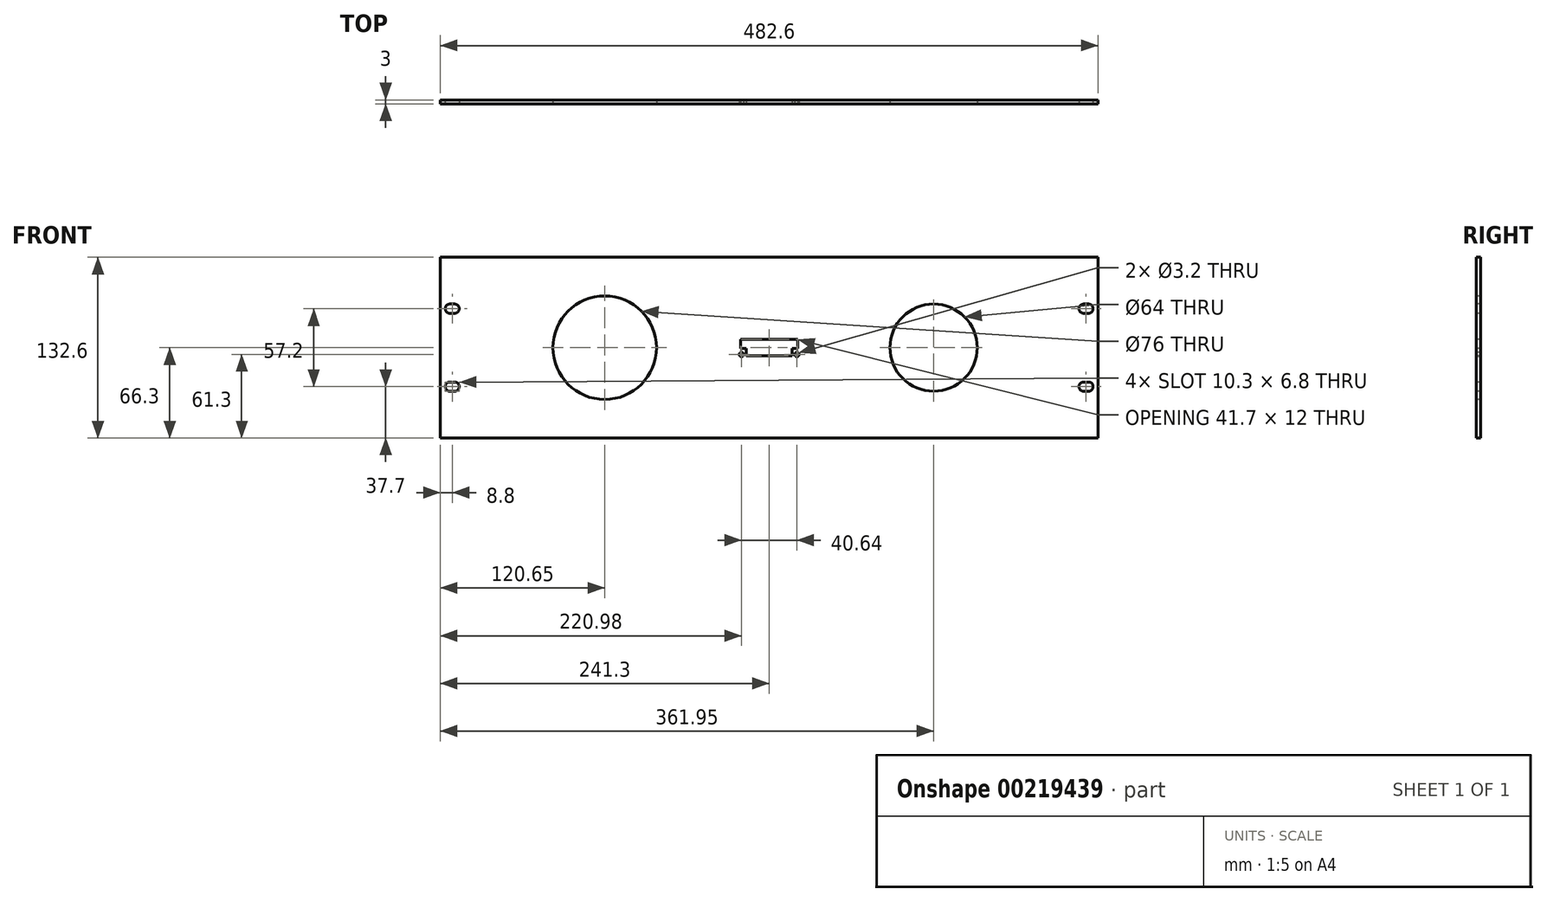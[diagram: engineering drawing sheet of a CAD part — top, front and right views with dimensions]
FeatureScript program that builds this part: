
annotation { "Feature Type Name" : "Feature", "Feature Type Description" : "" }
export const myFeature = defineFeature(function(context is Context, id is Id, definition is map)
    precondition{}
    {
        {
            var Q0;
            Q0=qCreatedBy(makeId("Front.planeOp"),FACE);
            var sketch = newSketch(context, id + "F0", { "sketchPlane" : qUnion([Q0])});
            skLineSegment(sketch, "E0.bottom", {"start": v(-241.3, 66.3) * mm, "end": v(241.3, 66.3) * mm});
            skLineSegment(sketch, "E0.top", {"start": v(-241.3, -66.3) * mm, "end": v(241.3, -66.3) * mm});
            skLineSegment(sketch, "E0.left", {"start": v(-241.3, 66.3) * mm, "end": v(-241.3, -66.3) * mm});
            skLineSegment(sketch, "E0.right", {"start": v(241.3, 66.3) * mm, "end": v(241.3, -66.3) * mm});
            skPoint(sketch, "E0.middle", {"position": v(0, 0) * mm});
            skSolve(sketch);
        }
        {
            var Q0;
            Q0=qSketchRegion(id+"F0",true);
            extrude(context, id + "F1", {"entities" : qUnion([Q0]), "oppositeDirection" : true, "depth" : 3 * mm});
        }
        {
            var Q0;
            Q0=makeQuery(id+"F1.opExtrude","CAP_FACE",FACE,{"disambiguationData":[OSD([sQuery(id+"F0.wireOp",EDGE,"E0.bottom"),sQuery(id+"F0.wireOp",EDGE,"E0.top"),sQuery(id+"F0.wireOp",EDGE,"E0.left"),sQuery(id+"F0.wireOp",EDGE,"E0.right")])],"isStart":true});
            var sketch = newSketch(context, id + "F2", { "sketchPlane" : qUnion([Q0])});
            skLineSegment(sketch, "E1.bottom", {"start": v(-230.75, 25.2) * mm, "end": v(-234.25, 25.2) * mm});
            skLineSegment(sketch, "E1.top", {"start": v(-230.75, 32) * mm, "end": v(-234.25, 32) * mm});
            skLineSegment(sketch, "E1.left", {"start": v(-230.75, 25.2) * mm, "end": v(-230.75, 32) * mm});
            skLineSegment(sketch, "E1.right", {"start": v(-234.25, 25.2) * mm, "end": v(-234.25, 32) * mm});
            skPoint(sketch, "E1.middle", {"position": v(-232.5, 28.6) * mm});
            skArc(sketch, "E2", {"start": v(-230.75, 25.2) * mm, "mid": v(-227.35, 28.6) * mm, "end": v(-230.75, 32) * mm});
            skArc(sketch, "E3", {"start": v(-234.25, 32) * mm, "mid": v(-237.65, 28.6) * mm, "end": v(-234.25, 25.2) * mm});
            skSolve(sketch);
        }
        {
            var Q0;
            Q0=makeQuery(id+"F2.imprint","IMPRINT",FACE,{"disambiguationData":[TD([[makeQuery(id+"F2.imprint","IMPRINT",EDGE,{"derivedFrom":sQuery(id+"F2.wireOp",EDGE,"E1.bottom")}),1.0]])]});
            var sketch = newSketch(context, id + "F3", { "sketchPlane" : qUnion([Q0])});
            skLineSegment(sketch, "E4.bottom", {"start": v(-230.75, -32) * mm, "end": v(-234.25, -32) * mm});
            skLineSegment(sketch, "E4.top", {"start": v(-230.75, -25.2) * mm, "end": v(-234.25, -25.2) * mm});
            skLineSegment(sketch, "E4.left", {"start": v(-230.75, -32) * mm, "end": v(-230.75, -25.2) * mm});
            skLineSegment(sketch, "E4.right", {"start": v(-234.25, -32) * mm, "end": v(-234.25, -25.2) * mm});
            skPoint(sketch, "E4.middle", {"position": v(-232.5, -28.6) * mm});
            skArc(sketch, "E5", {"start": v(-230.75, -32) * mm, "mid": v(-227.35, -28.6) * mm, "end": v(-230.75, -25.2) * mm});
            skArc(sketch, "E6", {"start": v(-234.25, -25.2) * mm, "mid": v(-237.65, -28.6) * mm, "end": v(-234.25, -32) * mm});
            skSolve(sketch);
        }
        {
            var Q0;
            Q0=makeQuery(id+"F2.imprint","IMPRINT",FACE,{"disambiguationData":[TD([[makeQuery(id+"F2.imprint","IMPRINT",EDGE,{"derivedFrom":sQuery(id+"F2.wireOp",EDGE,"E1.bottom")}),1.0]])]});
            var sketch = newSketch(context, id + "F4", { "sketchPlane" : qUnion([Q0])});
            skLineSegment(sketch, "E7.bottom", {"start": v(234.25, 32) * mm, "end": v(230.75, 32) * mm});
            skLineSegment(sketch, "E7.top", {"start": v(234.25, 25.2) * mm, "end": v(230.75, 25.2) * mm});
            skLineSegment(sketch, "E7.left", {"start": v(234.25, 32) * mm, "end": v(234.25, 25.2) * mm});
            skLineSegment(sketch, "E7.right", {"start": v(230.75, 32) * mm, "end": v(230.75, 25.2) * mm});
            skPoint(sketch, "E7.middle", {"position": v(232.5, 28.6) * mm});
            skArc(sketch, "E8", {"start": v(234.25, 25.2) * mm, "mid": v(237.65, 28.6) * mm, "end": v(234.25, 32) * mm});
            skArc(sketch, "E9", {"start": v(230.75, 32) * mm, "mid": v(227.35, 28.6) * mm, "end": v(230.75, 25.2) * mm});
            skSolve(sketch);
        }
        {
            var Q0;
            Q0=makeQuery(id+"F2.imprint","IMPRINT",FACE,{"disambiguationData":[TD([[makeQuery(id+"F2.imprint","IMPRINT",EDGE,{"derivedFrom":sQuery(id+"F2.wireOp",EDGE,"E1.bottom")}),1.0]])]});
            var sketch = newSketch(context, id + "F5", { "sketchPlane" : qUnion([Q0])});
            skLineSegment(sketch, "E10.bottom", {"start": v(234.25, -32) * mm, "end": v(230.75, -32) * mm});
            skLineSegment(sketch, "E10.top", {"start": v(234.25, -25.2) * mm, "end": v(230.75, -25.2) * mm});
            skLineSegment(sketch, "E10.left", {"start": v(234.25, -32) * mm, "end": v(234.25, -25.2) * mm});
            skLineSegment(sketch, "E10.right", {"start": v(230.75, -32) * mm, "end": v(230.75, -25.2) * mm});
            skPoint(sketch, "E10.middle", {"position": v(232.5, -28.6) * mm});
            skArc(sketch, "E11", {"start": v(230.75, -25.2) * mm, "mid": v(227.35, -28.6) * mm, "end": v(230.75, -32) * mm});
            skArc(sketch, "E12", {"start": v(234.25, -32) * mm, "mid": v(237.65, -28.6) * mm, "end": v(234.25, -25.2) * mm});
            skSolve(sketch);
        }
        {
            var Q0;
            Q0=qSketchRegion(id+"F2",true);
            var Q1;
            Q1=qSketchRegion(id+"F3",true);
            var Q2;
            Q2=qSketchRegion(id+"F4",true);
            var Q3;
            Q3=qSketchRegion(id+"F5",true);
            extrude(context, id + "F6", {"entities" : qUnion([Q0, Q1, Q2, Q3]), "operationType" : NewBodyOperationType.REMOVE, "oppositeDirection" : true, "depth" : 3 * mm});
        }
        {
            var Q0;
            Q0=makeQuery(id+"F1.opExtrude","CAP_FACE",FACE,{"disambiguationData":[OSD([sQuery(id+"F0.wireOp",EDGE,"E0.bottom"),sQuery(id+"F0.wireOp",EDGE,"E0.top"),sQuery(id+"F0.wireOp",EDGE,"E0.left"),sQuery(id+"F0.wireOp",EDGE,"E0.right")])],"isStart":true});
            var sketch = newSketch(context, id + "F7", { "sketchPlane" : qUnion([Q0])});
            skCircle(sketch, "E13", {"center": v(-120.65, 0) * mm, "radius": 38 * mm});
            skCircle(sketch, "E14", {"center": v(120.65, 0) * mm, "radius": 32 * mm});
            skLineSegment(sketch, "E15", {"start": v(20.85, 6) * mm, "end": v(-20.85, 6) * mm});
            skLineSegment(sketch, "E16", {"start": v(-20.85, 6) * mm, "end": v(-20.85, -0.5) * mm});
            skLineSegment(sketch, "E17", {"start": v(-20.85, -0.5) * mm, "end": v(-16.75, -0.5) * mm});
            skLineSegment(sketch, "E18", {"start": v(-16.75, -0.5) * mm, "end": v(-16.75, -6) * mm});
            skLineSegment(sketch, "E19", {"start": v(-16.75, -6) * mm, "end": v(16.75, -6) * mm});
            skLineSegment(sketch, "E20", {"start": v(16.75, -6) * mm, "end": v(16.75, -0.5) * mm});
            skLineSegment(sketch, "E21", {"start": v(16.75, -0.5) * mm, "end": v(20.85, -0.5) * mm});
            skLineSegment(sketch, "E22", {"start": v(20.85, -0.5) * mm, "end": v(20.85, 6) * mm});
            skCircle(sketch, "E23", {"center": v(20.32, -5) * mm, "radius": 1.6 * mm});
            skCircle(sketch, "E24", {"center": v(-20.32, -5) * mm, "radius": 1.6 * mm});
            skSolve(sketch);
        }
        {
            var Q0;
            Q0=qSketchRegion(id+"F7",true);
            extrude(context, id + "F8", {"entities" : qUnion([Q0]), "operationType" : NewBodyOperationType.REMOVE, "oppositeDirection" : true, "depth" : 3 * mm});
        }
    });
